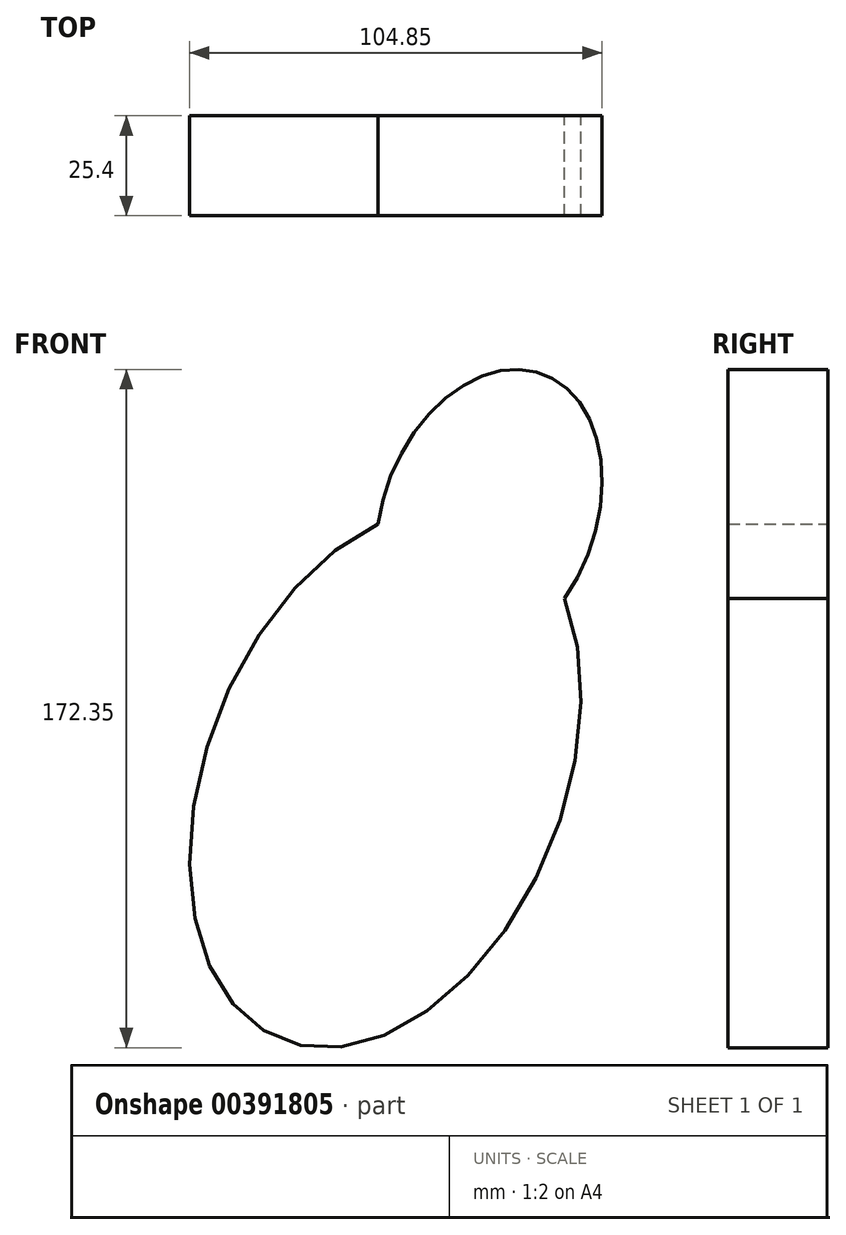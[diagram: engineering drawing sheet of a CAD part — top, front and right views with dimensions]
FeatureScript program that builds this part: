
annotation { "Feature Type Name" : "Feature", "Feature Type Description" : "" }
export const myFeature = defineFeature(function(context is Context, id is Id, definition is map)
    precondition{}
    {
        {
            var Q0;
            Q0=qCreatedBy(makeId("Front.planeOp"),FACE);
            var sketch = newSketch(context, id + "F0", { "sketchPlane" : qUnion([Q0])});
            skEllipse(sketch, "E0", {"center": v(26.37, 66.52) * mm, "majorRadius": 71.55 * mm, "minorRadius": 45.39 * mm, "majorAxis": v(-0.37, -0.93)});
            skEllipse(sketch, "E1", {"center": v(52.74, 133.03) * mm, "majorRadius": 38.56 * mm, "minorRadius": 26.93 * mm, "majorAxis": v(-0.36, -0.93)});
            skSolve(sketch);
        }
        {
            var Q0;
            Q0 = qSketchRegion(id + "F0", true);
            extrude(context, id + "F1", {"entities" : qUnion([Q0]), "depth" : 25.4 * mm});
        }
    });
